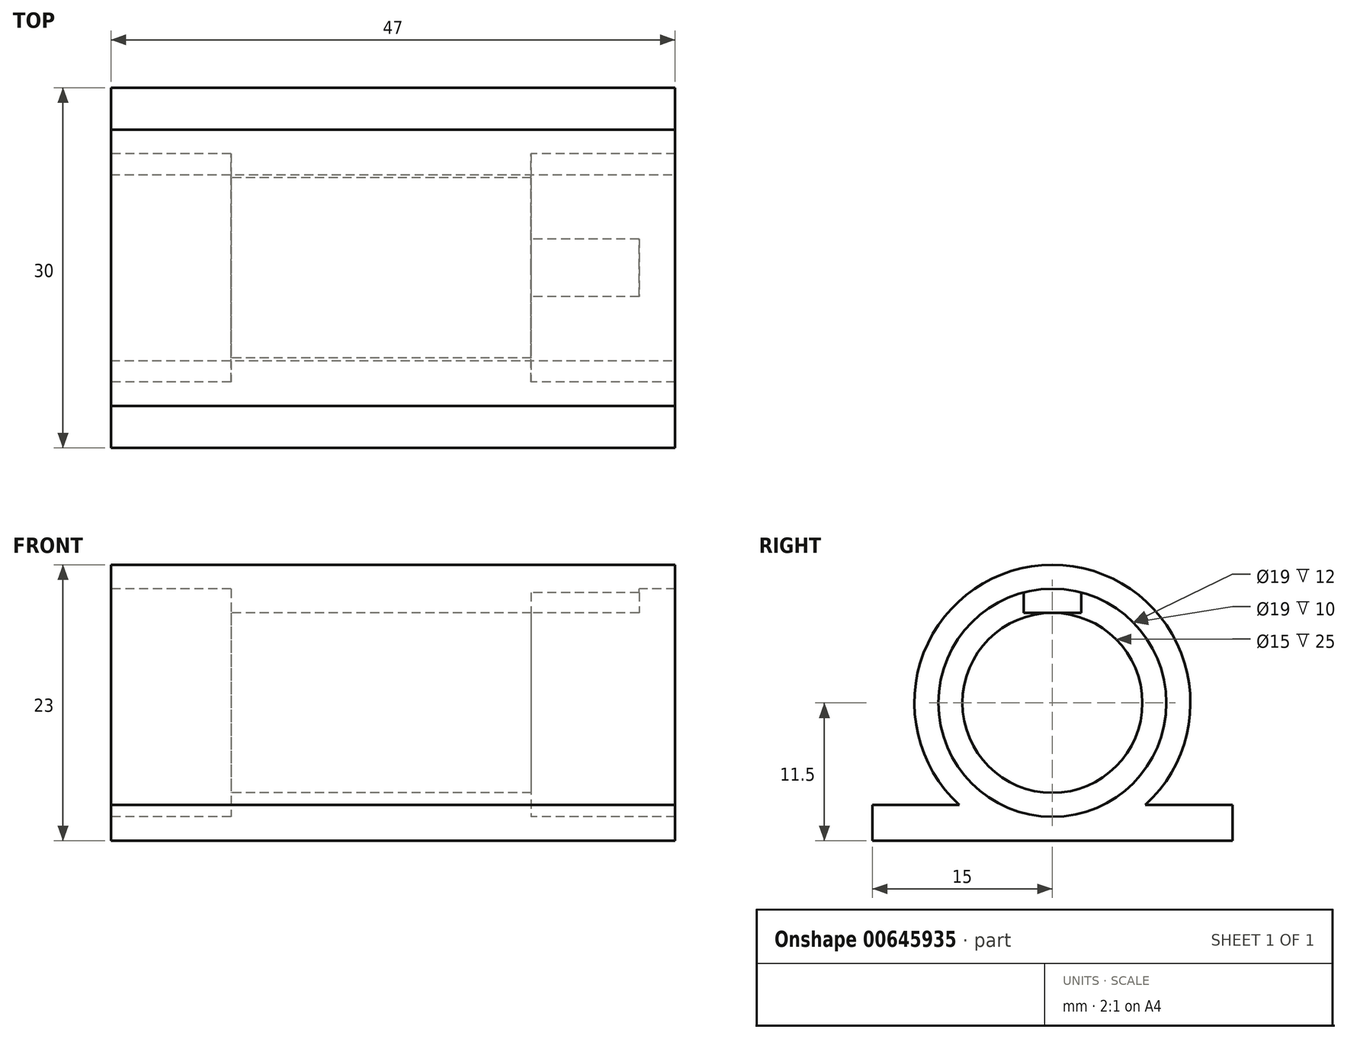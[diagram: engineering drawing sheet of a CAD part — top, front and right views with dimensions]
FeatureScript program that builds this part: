
annotation { "Feature Type Name" : "Feature", "Feature Type Description" : "" }
export const myFeature = defineFeature(function(context is Context, id is Id, definition is map)
    precondition{}
    {
        {
            var Q0;
            Q0=qCreatedBy(makeId("Front.planeOp"),FACE);
            var sketch = newSketch(context, id + "F0", { "sketchPlane" : qUnion([Q0])});
            skLineSegment(sketch, "E0", {"start": v(-54.5, 0) * mm, "end": v(60.13, 0) * mm, "construction": true});
            skLineSegment(sketch, "E1", {"start": v(-5.66, 7.5) * mm, "end": v(19.34, 7.5) * mm});
            skLineSegment(sketch, "E2", {"start": v(19.34, 7.5) * mm, "end": v(19.34, 9.5) * mm});
            skLineSegment(sketch, "E3", {"start": v(19.34, 9.5) * mm, "end": v(31.34, 9.5) * mm});
            skLineSegment(sketch, "E4", {"start": v(31.34, 11.5) * mm, "end": v(-15.66, 11.5) * mm});
            skLineSegment(sketch, "E5", {"start": v(-15.66, 11.5) * mm, "end": v(-15.66, 9.5) * mm});
            skLineSegment(sketch, "E6", {"start": v(-15.66, 9.5) * mm, "end": v(-5.66, 9.5) * mm});
            skLineSegment(sketch, "E7", {"start": v(-5.66, 9.5) * mm, "end": v(-5.66, 7.5) * mm});
            skLineSegment(sketch, "E8", {"start": v(31.34, 9.5) * mm, "end": v(31.34, 11.5) * mm});
            skSolve(sketch);
        }
        {
            var Q0;
            Q0=makeQuery(id+"F0.imprint","IMPRINT",FACE,{"disambiguationData":[TD([[makeQuery(id+"F0.imprint","IMPRINT",EDGE,{"derivedFrom":sQuery(id+"F0.wireOp",EDGE,"E1")}),1.0]])]});
            var Q1;
            Q1=sQuery(id+"F0.wireOp",EDGE,"E0");
            revolve(context, id + "F1", {"entities" : qUnion([Q0]), "axis" : qUnion([Q1]), "revolveType" : RevolveType.FULL});
        }
        {
            var Q0;
            Q0=makeQuery(id+"F1.opRevolve","SWEPT_FACE",FACE,{"disambiguationData":[OSD([sQuery(id+"F0.wireOp",EDGE,"E2")])]});
            var sketch = newSketch(context, id + "F2", { "sketchPlane" : qUnion([Q0])});
            skLineSegment(sketch, "E9.bottom", {"start": v(0, 9.5) * mm, "end": v(2.4, 9.5) * mm});
            skLineSegment(sketch, "E9.left", {"start": v(0, 9.5) * mm, "end": v(0, 7.5) * mm});
            skLineSegment(sketch, "E9.right", {"start": v(2.4, 9.5) * mm, "end": v(2.4, 7.5) * mm});
            skLineSegment(sketch, "E10.MirrorCS", {"start": v(-2.4, 9.5) * mm, "end": v(-2.4, 7.5) * mm});
            skLineSegment(sketch, "E11", {"start": v(0, 7.5) * mm, "end": v(2.4, 7.5) * mm});
            skLineSegment(sketch, "E12", {"start": v(2.4, 7.5) * mm, "end": v(-2.4, 7.5) * mm});
            skSolve(sketch);
        }
        {
            var Q0;
            {var subQ0=sQuery(id+"F2.wireOp",EDGE,"E9.left");Q0=makeQuery(id+"F2.imprint","IMPRINT",FACE,{"disambiguationData":[TD([[makeQuery(id+"F2.imprint","IMPRINT",EDGE,{"derivedFrom":subQ0}),-1.0]])]});}
            var Q1;
            {var subQ0=sQuery(id+"F2.wireOp",EDGE,"E9.left");Q1=makeQuery(id+"F2.imprint","IMPRINT",FACE,{"disambiguationData":[TD([[makeQuery(id+"F2.imprint","IMPRINT",EDGE,{"derivedFrom":subQ0}),1.0]])]});}
            extrude(context, id + "F3", {"entities" : qUnion([Q0, Q1]), "operationType" : NewBodyOperationType.ADD, "depth" : 9 * mm, "offsetDistance" : 25 * mm});
        }
        {
            var Q0;
            Q0=makeQuery(id+"F1.opRevolve","SWEPT_FACE",FACE,{"disambiguationData":[OSD([sQuery(id+"F0.wireOp",EDGE,"E8")])]});
            var sketch = newSketch(context, id + "F4", { "sketchPlane" : qUnion([Q0])});
            skLineSegment(sketch, "E13.bottom", {"start": v(0, -11.5) * mm, "end": v(15, -11.5) * mm});
            skLineSegment(sketch, "E13.top", {"start": v(0, -8.5) * mm, "end": v(15, -8.5) * mm});
            skLineSegment(sketch, "E13.left", {"start": v(0, -11.5) * mm, "end": v(0, -8.5) * mm});
            skLineSegment(sketch, "E13.right", {"start": v(15, -11.5) * mm, "end": v(15, -8.5) * mm});
            skLineSegment(sketch, "E14.MirrorCS", {"start": v(-15, -11.5) * mm, "end": v(-15, -8.5) * mm});
            skLineSegment(sketch, "E15.MirrorCS", {"start": v(0, -8.5) * mm, "end": v(-15, -8.5) * mm});
            skLineSegment(sketch, "E16.MirrorCS", {"start": v(0, -11.5) * mm, "end": v(-15, -11.5) * mm});
            skSolve(sketch);
        }
        {
            var Q0;
            {var subQ0=sQuery(id+"F4.wireOp",EDGE,"E14.MirrorCS");Q0=makeQuery(id+"F4.imprint","IMPRINT",FACE,{"disambiguationData":[TD([[makeQuery(id+"F4.imprint","IMPRINT",EDGE,{"derivedFrom":subQ0}),-1.0]])]});}
            var Q1;
            {var subQ0=sQuery(id+"F4.wireOp",EDGE,"E13.bottom");Q1=makeQuery(id+"F4.imprint","IMPRINT",FACE,{"disambiguationData":[TD([[makeQuery(id+"F4.imprint","IMPRINT",EDGE,{"derivedFrom":subQ0}),1.0]])]});}
            var Q2;
            Q2=makeQuery(id+"F1.opRevolve","SWEPT_FACE",FACE,{"disambiguationData":[OSD([sQuery(id+"F0.wireOp",EDGE,"E5")])]});
            extrude(context, id + "F5", {"entities" : qUnion([Q0, Q1]), "operationType" : NewBodyOperationType.ADD, "endBound" : BoundingType.UP_TO_SURFACE, "oppositeDirection" : true, "depth" : 25 * mm, "endBoundEntityFace" : qUnion([Q2]), "offsetDistance" : 25 * mm});
        }
    });
